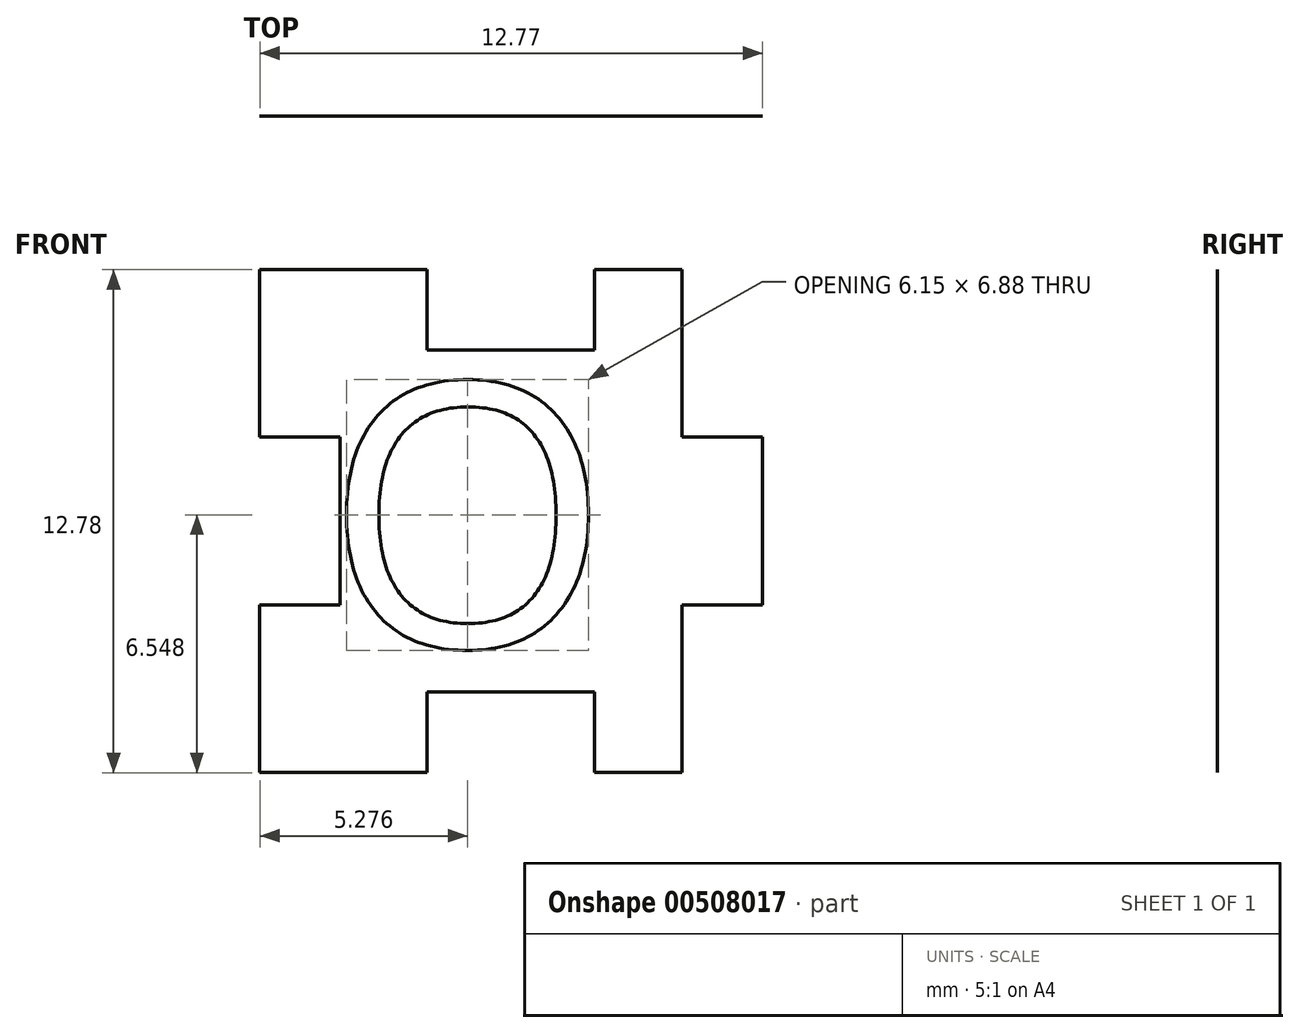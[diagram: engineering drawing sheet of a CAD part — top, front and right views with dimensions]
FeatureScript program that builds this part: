
annotation { "Feature Type Name" : "Feature", "Feature Type Description" : "" }
export const myFeature = defineFeature(function(context is Context, id is Id, definition is map)
    precondition{}
    {
        {
            var Q0;
            Q0=qCreatedBy(makeId("Front.planeOp"),FACE);
            var sketch = newSketch(context, id + "F0", { "sketchPlane" : qUnion([Q0])});
            skLineSegment(sketch, "E0", {"start": v(-10.99, 26.89) * mm, "end": v(-10.99, 29.02) * mm});
            skLineSegment(sketch, "E1", {"start": v(-10.99, 29.02) * mm, "end": v(-13.03, 29.02) * mm});
            skLineSegment(sketch, "E2", {"start": v(-13.03, 29.02) * mm, "end": v(-13.03, 33.28) * mm});
            skLineSegment(sketch, "E3", {"start": v(-13.03, 33.28) * mm, "end": v(-8.78, 33.28) * mm});
            skLineSegment(sketch, "E4", {"start": v(-8.78, 33.28) * mm, "end": v(-8.78, 31.23) * mm});
            skLineSegment(sketch, "E5", {"start": v(-8.78, 31.23) * mm, "end": v(-4.53, 31.23) * mm});
            skLineSegment(sketch, "E6", {"start": v(-4.53, 31.23) * mm, "end": v(-4.53, 33.28) * mm});
            skLineSegment(sketch, "E7", {"start": v(-4.53, 33.28) * mm, "end": v(-2.3, 33.28) * mm});
            skLineSegment(sketch, "E8", {"start": v(-2.3, 33.28) * mm, "end": v(-2.3, 29.02) * mm});
            skLineSegment(sketch, "E9", {"start": v(-2.3, 29.02) * mm, "end": v(-0.26, 29.02) * mm});
            skLineSegment(sketch, "E10", {"start": v(-10.99, 26.89) * mm, "end": v(8.72, 26.89) * mm, "construction": true});
            skLineSegment(sketch, "E11.MirrorCS", {"start": v(-2.3, 24.76) * mm, "end": v(-0.26, 24.76) * mm});
            skLineSegment(sketch, "E12.MirrorCS", {"start": v(-2.3, 20.5) * mm, "end": v(-2.3, 24.76) * mm});
            skLineSegment(sketch, "E13.MirrorCS", {"start": v(-4.53, 20.5) * mm, "end": v(-2.3, 20.5) * mm});
            skLineSegment(sketch, "E14.MirrorCS", {"start": v(-4.53, 22.55) * mm, "end": v(-4.53, 20.5) * mm});
            skLineSegment(sketch, "E15.MirrorCS", {"start": v(-8.78, 22.55) * mm, "end": v(-4.53, 22.55) * mm});
            skLineSegment(sketch, "E16.MirrorCS", {"start": v(-8.78, 20.5) * mm, "end": v(-8.78, 22.55) * mm});
            skLineSegment(sketch, "E17.MirrorCS", {"start": v(-13.03, 20.5) * mm, "end": v(-8.78, 20.5) * mm});
            skLineSegment(sketch, "E18.MirrorCS", {"start": v(-13.03, 24.76) * mm, "end": v(-13.03, 20.5) * mm});
            skLineSegment(sketch, "E19.MirrorCS", {"start": v(-10.99, 24.76) * mm, "end": v(-13.03, 24.76) * mm});
            skLineSegment(sketch, "E20.MirrorCS", {"start": v(-10.99, 26.89) * mm, "end": v(-10.99, 24.76) * mm});
            skLineSegment(sketch, "E21", {"start": v(-0.26, 29.02) * mm, "end": v(-0.26, 24.76) * mm});
            skSolve(sketch);
        }
        {
            var Q0;
            Q0=makeQuery(id+"F0.imprint","IMPRINT",FACE,{"disambiguationData":[TD([[makeQuery(id+"F0.imprint","IMPRINT",EDGE,{"derivedFrom":sQuery(id+"F0.wireOp",EDGE,"E0")}),-1.0]])]});
            extrude(context, id + "F1", {"entities" : qUnion([Q0]), "depth" : .16 / 50.8 * mm, "offsetDistance" : 25 * mm});
        }
        {
            var Q0;
            Q0=makeQuery(id+"F1.opExtrude","CAP_FACE",FACE,{"disambiguationData":[OSD([sQuery(id+"F0.wireOp",EDGE,"E0"),sQuery(id+"F0.wireOp",EDGE,"E1"),sQuery(id+"F0.wireOp",EDGE,"E2"),sQuery(id+"F0.wireOp",EDGE,"E3"),sQuery(id+"F0.wireOp",EDGE,"E4"),sQuery(id+"F0.wireOp",EDGE,"E5"),sQuery(id+"F0.wireOp",EDGE,"E6"),sQuery(id+"F0.wireOp",EDGE,"E7"),sQuery(id+"F0.wireOp",EDGE,"E8"),sQuery(id+"F0.wireOp",EDGE,"E9"),sQuery(id+"F0.wireOp",EDGE,"E11.MirrorCS"),sQuery(id+"F0.wireOp",EDGE,"E12.MirrorCS"),sQuery(id+"F0.wireOp",EDGE,"E13.MirrorCS"),sQuery(id+"F0.wireOp",EDGE,"E14.MirrorCS"),sQuery(id+"F0.wireOp",EDGE,"E15.MirrorCS"),sQuery(id+"F0.wireOp",EDGE,"E16.MirrorCS"),sQuery(id+"F0.wireOp",EDGE,"E17.MirrorCS"),sQuery(id+"F0.wireOp",EDGE,"E18.MirrorCS"),sQuery(id+"F0.wireOp",EDGE,"E19.MirrorCS"),sQuery(id+"F0.wireOp",EDGE,"E20.MirrorCS"),sQuery(id+"F0.wireOp",EDGE,"E21")])],"isStart":false});
            var sketch = newSketch(context, id + "F2", { "sketchPlane" : qUnion([Q0])});
            skText(sketch, "E22", { "text": "O", "fontName": "OpenSans-Regular.ttf"});
            skPoint(sketch, "E23", {"position": v(-6.65, 22.55) * mm});
            const initialGuessF2  = {"E22": [-0.0114, 0.0237, 1, 0, 0.00674]};
            skSetInitialGuess(sketch, initialGuessF2);
            skSolve(sketch);
        }
        {
            var Q0;
            Q0=makeQuery(id+"F2.imprint","IMPRINT",FACE,{"disambiguationData":[TD([[makeQuery(id+"F2.imprint","IMPRINT",EDGE,{"derivedFrom":sQuery(id+"F2.wireOp",EDGE,"E22.sketch_text.stroke-0")}),-1.0]])]});
            extrude(context, id + "F3", {"entities" : qUnion([Q0]), "operationType" : NewBodyOperationType.REMOVE, "oppositeDirection" : true, "depth" : 1 * mm, "offsetDistance" : 25 * mm});
        }
    });
